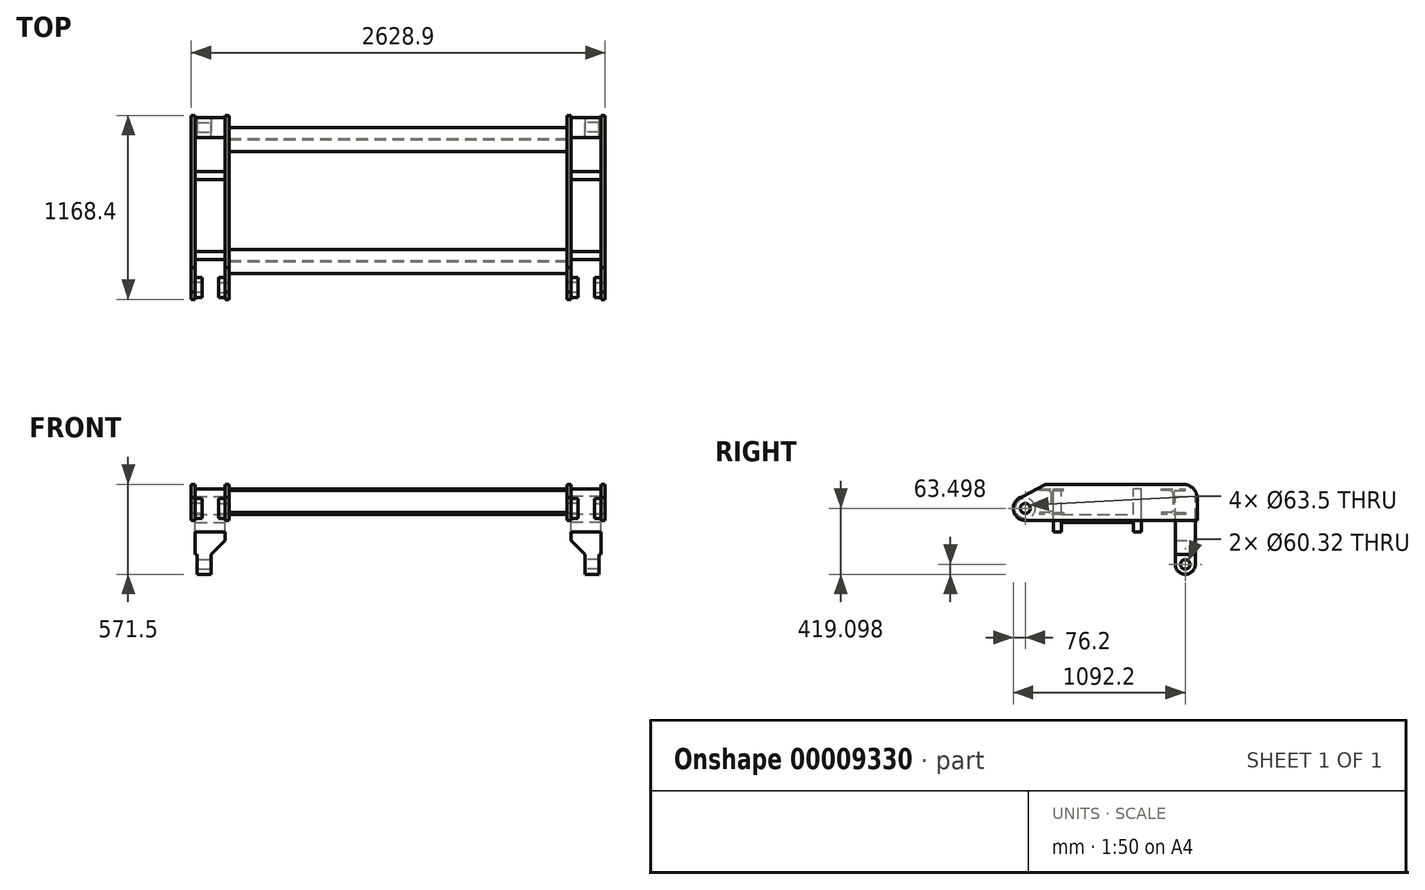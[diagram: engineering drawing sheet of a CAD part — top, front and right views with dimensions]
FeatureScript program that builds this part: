
annotation { "Feature Type Name" : "Feature", "Feature Type Description" : "" }
export const myFeature = defineFeature(function(context is Context, id is Id, definition is map)
    precondition{}
    {
        {
            var Q0;
            Q0=qCreatedBy(makeId("Right.planeOp"),FACE);
            var sketch = newSketch(context, id + "F0", { "sketchPlane" : qUnion([Q0])});
            skLineSegment(sketch, "E0", {"start": v(0, 94.66) * mm, "end": v(0, -108.5) * mm, "construction": true});
            skLineSegment(sketch, "E1.0", {"start": v(387.35, 94.66) * mm, "end": v(387.35, -76.51) * mm, "construction": true});
            skLineSegment(sketch, "E2", {"start": v(387.35, -6.92) * mm, "end": v(515.37, -6.92) * mm, "construction": true});
            skLineSegment(sketch, "E3.0", {"start": v(391.16, 49.98) * mm, "end": v(391.16, -63.81) * mm});
            skLineSegment(sketch, "E4.0", {"start": v(387.35, -87.94) * mm, "end": v(463.55, -87.94) * mm});
            skLineSegment(sketch, "E5.0", {"start": v(403.86, -76.51) * mm, "end": v(463.55, -76.51) * mm});
            skLineSegment(sketch, "E6.trimOffspring", {"start": v(463.55, -76.51) * mm, "end": v(463.55, -87.94) * mm});
            skLineSegment(sketch, "E7.0.MirrorCS", {"start": v(463.55, 62.68) * mm, "end": v(463.55, 74.11) * mm});
            skLineSegment(sketch, "E7.1.MirrorCS", {"start": v(387.35, 74.11) * mm, "end": v(463.55, 74.11) * mm});
            skLineSegment(sketch, "E7.2.MirrorCS", {"start": v(403.86, 62.68) * mm, "end": v(463.55, 62.68) * mm});
            skPoint(sketch, "E8.trimOffspring.end.orphan", {"position": v(387.35, -108.5) * mm});
            skLineSegment(sketch, "E9.0.MirrorCS", {"start": v(311.15, 62.68) * mm, "end": v(311.15, 74.11) * mm});
            skLineSegment(sketch, "E9.1.MirrorCS", {"start": v(311.15, -76.51) * mm, "end": v(311.15, -87.94) * mm});
            skLineSegment(sketch, "E9.2.MirrorCS", {"start": v(387.35, -87.94) * mm, "end": v(311.15, -87.94) * mm});
            skLineSegment(sketch, "E9.3.MirrorCS", {"start": v(383.54, 49.98) * mm, "end": v(383.54, -63.81) * mm});
            skLineSegment(sketch, "E9.4.MirrorCS", {"start": v(387.35, 74.11) * mm, "end": v(311.15, 74.11) * mm});
            skLineSegment(sketch, "E9.5.MirrorCS", {"start": v(370.84, 62.68) * mm, "end": v(311.15, 62.68) * mm});
            skLineSegment(sketch, "E9.6.MirrorCS", {"start": v(370.84, -76.51) * mm, "end": v(311.15, -76.51) * mm});
            skPoint(sketch, "E10.visualSharp", {"position": v(383.54, 62.68) * mm});
            skArc(sketch, "E10.filletArc", {"start": v(383.54, 49.98) * mm, "mid": v(379.82, 58.96) * mm, "end": v(370.84, 62.68) * mm});
            skPoint(sketch, "E11.visualSharp", {"position": v(391.16, 62.68) * mm});
            skArc(sketch, "E11.filletArc", {"start": v(403.86, 62.68) * mm, "mid": v(394.88, 58.96) * mm, "end": v(391.16, 49.98) * mm});
            skPoint(sketch, "E12.visualSharp", {"position": v(383.54, -76.51) * mm});
            skArc(sketch, "E12.filletArc", {"start": v(370.84, -76.51) * mm, "mid": v(379.82, -72.8) * mm, "end": v(383.54, -63.81) * mm});
            skPoint(sketch, "E13.visualSharp", {"position": v(391.16, -76.51) * mm});
            skArc(sketch, "E13.filletArc", {"start": v(391.16, -63.81) * mm, "mid": v(394.88, -72.8) * mm, "end": v(403.86, -76.51) * mm});
            skArc(sketch, "E14.0.MirrorCS", {"start": v(-403.86, 62.68) * mm, "mid": v(-394.88, 58.96) * mm, "end": v(-391.16, 49.98) * mm});
            skArc(sketch, "E14.1.MirrorCS", {"start": v(-391.16, -63.81) * mm, "mid": v(-394.88, -72.8) * mm, "end": v(-403.86, -76.51) * mm});
            skLineSegment(sketch, "E14.2.MirrorCS", {"start": v(-311.15, 62.68) * mm, "end": v(-311.15, 74.11) * mm});
            skArc(sketch, "E14.3.MirrorCS", {"start": v(-383.54, 49.98) * mm, "mid": v(-379.82, 58.96) * mm, "end": v(-370.84, 62.68) * mm});
            skArc(sketch, "E14.4.MirrorCS", {"start": v(-370.84, -76.51) * mm, "mid": v(-379.82, -72.8) * mm, "end": v(-383.54, -63.81) * mm});
            skLineSegment(sketch, "E14.5.MirrorCS", {"start": v(-311.15, -76.51) * mm, "end": v(-311.15, -87.94) * mm});
            skLineSegment(sketch, "E14.6.MirrorCS", {"start": v(-463.55, 62.68) * mm, "end": v(-463.55, 74.11) * mm});
            skLineSegment(sketch, "E14.7.MirrorCS", {"start": v(-463.55, -76.51) * mm, "end": v(-463.55, -87.94) * mm});
            skLineSegment(sketch, "E14.8.MirrorCS", {"start": v(-387.35, 94.66) * mm, "end": v(-387.35, -76.51) * mm, "construction": true});
            skPoint(sketch, "E14.9.MirrorP", {"position": v(-391.16, -76.51) * mm});
            skLineSegment(sketch, "E14.10.MirrorCS", {"start": v(-370.84, -76.51) * mm, "end": v(-311.15, -76.51) * mm});
            skPoint(sketch, "E14.11.MirrorP", {"position": v(-387.35, -108.5) * mm});
            skLineSegment(sketch, "E14.12.MirrorCS", {"start": v(-383.54, 49.98) * mm, "end": v(-383.54, -63.81) * mm});
            skPoint(sketch, "E14.13.MirrorP", {"position": v(-391.16, 62.68) * mm});
            skLineSegment(sketch, "E14.14.MirrorCS", {"start": v(-403.86, 62.68) * mm, "end": v(-463.55, 62.68) * mm});
            skLineSegment(sketch, "E14.15.MirrorCS", {"start": v(-403.86, -76.51) * mm, "end": v(-463.55, -76.51) * mm});
            skLineSegment(sketch, "E14.16.MirrorCS", {"start": v(-370.84, 62.68) * mm, "end": v(-311.15, 62.68) * mm});
            skLineSegment(sketch, "E14.17.MirrorCS", {"start": v(-387.35, 74.11) * mm, "end": v(-463.55, 74.11) * mm});
            skLineSegment(sketch, "E14.18.MirrorCS", {"start": v(-387.35, 74.11) * mm, "end": v(-311.15, 74.11) * mm});
            skPoint(sketch, "E14.19.MirrorP", {"position": v(-383.54, -76.51) * mm});
            skLineSegment(sketch, "E14.20.MirrorCS", {"start": v(-387.35, -87.94) * mm, "end": v(-463.55, -87.94) * mm});
            skPoint(sketch, "E14.21.MirrorP", {"position": v(-383.54, 62.68) * mm});
            skLineSegment(sketch, "E14.22.MirrorCS", {"start": v(-387.35, -87.94) * mm, "end": v(-311.15, -87.94) * mm});
            skLineSegment(sketch, "E14.23.MirrorCS", {"start": v(-391.16, 49.98) * mm, "end": v(-391.16, -63.81) * mm});
            skSolve(sketch);
        }
        {
            var Q0;
            Q0 = qSketchRegion(id + "F0", true);
            extrude(context, id + "F1", {"entities" : qUnion([Q0]), "endBound" : BoundingType.SYMMETRIC, "depth" : 2146.3 * mm});
        }
        {
            var Q0;
            Q0=makeQuery(id+"F1.opExtrude","CAP_FACE",FACE,{"disambiguationData":[OSD([sQuery(id+"F0.wireOp",EDGE,"E14.0.MirrorCS"),sQuery(id+"F0.wireOp",EDGE,"E14.1.MirrorCS"),sQuery(id+"F0.wireOp",EDGE,"E14.2.MirrorCS"),sQuery(id+"F0.wireOp",EDGE,"E14.3.MirrorCS"),sQuery(id+"F0.wireOp",EDGE,"E14.4.MirrorCS"),sQuery(id+"F0.wireOp",EDGE,"E14.5.MirrorCS"),sQuery(id+"F0.wireOp",EDGE,"E14.6.MirrorCS"),sQuery(id+"F0.wireOp",EDGE,"E14.7.MirrorCS"),sQuery(id+"F0.wireOp",EDGE,"E14.10.MirrorCS"),sQuery(id+"F0.wireOp",EDGE,"E14.12.MirrorCS"),sQuery(id+"F0.wireOp",EDGE,"E14.14.MirrorCS"),sQuery(id+"F0.wireOp",EDGE,"E14.15.MirrorCS"),sQuery(id+"F0.wireOp",EDGE,"E14.16.MirrorCS"),sQuery(id+"F0.wireOp",EDGE,"E14.17.MirrorCS"),sQuery(id+"F0.wireOp",EDGE,"E14.18.MirrorCS"),sQuery(id+"F0.wireOp",EDGE,"E14.20.MirrorCS"),sQuery(id+"F0.wireOp",EDGE,"E14.22.MirrorCS"),sQuery(id+"F0.wireOp",EDGE,"E14.23.MirrorCS")])],"isStart":false});
            var sketch = newSketch(context, id + "F2", { "sketchPlane" : qUnion([Q0])});
            skLineSegment(sketch, "E15.0", {"start": v(311.15, 74.11) * mm, "end": v(463.55, 74.11) * mm, "construction": true});
            skLineSegment(sketch, "E16", {"start": v(387.35, 74.11) * mm, "end": v(387.35, -187.68) * mm, "construction": true});
            skLineSegment(sketch, "E17", {"start": v(539.75, 13.66) * mm, "end": v(539.75, -126.04) * mm});
            skLineSegment(sketch, "E18.0", {"start": v(450.85, 102.56) * mm, "end": v(-425.45, 102.56) * mm});
            skPoint(sketch, "E19.visualSharp", {"position": v(539.75, 102.56) * mm});
            skArc(sketch, "E19.filletArc", {"start": v(539.75, 13.66) * mm, "mid": v(513.71, 76.52) * mm, "end": v(450.85, 102.56) * mm});
            skLineSegment(sketch, "E20.0", {"start": v(-628.65, 13.66) * mm, "end": v(-628.65, -213.35) * mm});
            skLineSegment(sketch, "E21.0", {"start": v(-552.45, -49.84) * mm, "end": v(-552.45, -126.04) * mm});
            skLineSegment(sketch, "E22", {"start": v(-424, -87.94) * mm, "end": v(-671.77, -87.94) * mm, "construction": true});
            skLineSegment(sketch, "E23.0", {"start": v(-424, -49.84) * mm, "end": v(-425.45, -49.84) * mm});
            skArc(sketch, "E24", {"start": v(-580.33, 21.07) * mm, "mid": v(-627.32, -64.03) * mm, "end": v(-552.45, -126.04) * mm});
            skLineSegment(sketch, "E25", {"start": v(-425.45, 102.56) * mm, "end": v(-595.1, 13.3) * mm});
            skLineSegment(sketch, "E26", {"start": v(-552.45, -126.04) * mm, "end": v(539.75, -126.04) * mm});
            skLineSegment(sketch, "E27.trimOffspring", {"start": v(-628.65, -49.84) * mm, "end": v(-671.77, -49.84) * mm});
            skCircle(sketch, "E28", {"center": v(-552.45, -49.84) * mm, "radius": 31.75 * mm});
            skSolve(sketch);
        }
        {
            var Q0;
            Q0 = qSketchRegion(id + "F2", true);
            extrude(context, id + "F3", {"entities" : qUnion([Q0]), "depth" : 25.4 * mm});
        }
        {
            var Q0;
            Q0=makeQuery(id+"F3.opExtrude","CAP_FACE",FACE,{"disambiguationData":[OSD([sQuery(id+"F2.wireOp",EDGE,"E17"),sQuery(id+"F2.wireOp",EDGE,"E18.0"),sQuery(id+"F2.wireOp",EDGE,"E19.filletArc"),sQuery(id+"F2.wireOp",EDGE,"E24"),sQuery(id+"F2.wireOp",EDGE,"E25"),sQuery(id+"F2.wireOp",EDGE,"E26"),sQuery(id+"F2.wireOp",EDGE,"E28")])],"isStart":false});
            var sketch = newSketch(context, id + "F4", { "sketchPlane" : qUnion([Q0])});
            skCircle(sketch, "E29", {"center": v(-552.45, -49.84) * mm, "radius": 63.5 * mm});
            skCircle(sketch, "E30.0", {"center": v(-552.45, -49.84) * mm, "radius": 31.75 * mm});
            skSolve(sketch);
        }
        {
            var Q0;
            Q0 = qSketchRegion(id + "F4", true);
            extrude(context, id + "F5", {"entities" : qUnion([Q0]), "operationType" : NewBodyOperationType.ADD, "depth" : 43.69 * mm});
        }
        {
            var Q0;
            Q0=makeQuery(id+"F3.opExtrude","CAP_FACE",FACE,{"disambiguationData":[OSD([sQuery(id+"F2.wireOp",EDGE,"E17"),sQuery(id+"F2.wireOp",EDGE,"E18.0"),sQuery(id+"F2.wireOp",EDGE,"E19.filletArc"),sQuery(id+"F2.wireOp",EDGE,"E24"),sQuery(id+"F2.wireOp",EDGE,"E25"),sQuery(id+"F2.wireOp",EDGE,"E26"),sQuery(id+"F2.wireOp",EDGE,"E28")])],"isStart":false});
            var sketch = newSketch(context, id + "F6", { "sketchPlane" : qUnion([Q0])});
            skLineSegment(sketch, "E31.0", {"start": v(311.15, 74.11) * mm, "end": v(463.55, 74.11) * mm, "construction": true});
            skLineSegment(sketch, "E32", {"start": v(387.35, 74.11) * mm, "end": v(387.35, 301) * mm, "construction": true});
            skLineSegment(sketch, "E33", {"start": v(184.15, 74.11) * mm, "end": v(133.35, 74.11) * mm});
            skLineSegment(sketch, "E34", {"start": v(463.55, 74.11) * mm, "end": v(463.55, 349.58) * mm, "construction": true});
            skLineSegment(sketch, "E35.0", {"start": v(-95.25, 74.11) * mm, "end": v(-95.25, 349.58) * mm, "construction": true});
            skLineSegment(sketch, "E36.0", {"start": v(133.35, -198.94) * mm, "end": v(133.35, -138.74) * mm});
            skLineSegment(sketch, "E37.0", {"start": v(184.15, -198.94) * mm, "end": v(184.15, 74.11) * mm});
            skLineSegment(sketch, "E38.0", {"start": v(184.15, -198.94) * mm, "end": v(133.35, -198.94) * mm});
            skLineSegment(sketch, "E39", {"start": v(-552.45, -49.84) * mm, "end": v(714.62, -49.84) * mm, "construction": true});
            skLineSegment(sketch, "E40.0", {"start": v(-323.85, -138.74) * mm, "end": v(133.35, -138.74) * mm});
            skLineSegment(sketch, "E41.0", {"start": v(-323.85, -87.94) * mm, "end": v(133.35, -87.94) * mm});
            skLineSegment(sketch, "E42.0.MirrorCS", {"start": v(-323.85, -198.94) * mm, "end": v(-323.85, -138.74) * mm});
            skLineSegment(sketch, "E42.1.MirrorCS", {"start": v(-374.65, -198.94) * mm, "end": v(-374.65, 74.11) * mm});
            skLineSegment(sketch, "E42.2.MirrorCS", {"start": v(-374.65, 74.11) * mm, "end": v(-323.85, 74.11) * mm});
            skLineSegment(sketch, "E42.3.MirrorCS", {"start": v(-374.65, -198.94) * mm, "end": v(-323.85, -198.94) * mm});
            skLineSegment(sketch, "E43.trimOffspring", {"start": v(-323.85, -87.94) * mm, "end": v(-323.85, 74.11) * mm});
            skLineSegment(sketch, "E44.trimOffspring", {"start": v(133.35, -87.94) * mm, "end": v(133.35, 74.11) * mm});
            skSolve(sketch);
        }
        {
            var Q0;
            Q0 = qSketchRegion(id + "F6", true);
            extrude(context, id + "F7", {"entities" : qUnion([Q0]), "depth" : 190.5 * mm});
        }
        {
            var Q0;
            Q0=makeQuery(id+"F3.opExtrude","CAP_FACE",FACE,{"disambiguationData":[OSD([sQuery(id+"F2.wireOp",EDGE,"E17"),sQuery(id+"F2.wireOp",EDGE,"E18.0"),sQuery(id+"F2.wireOp",EDGE,"E19.filletArc"),sQuery(id+"F2.wireOp",EDGE,"E24"),sQuery(id+"F2.wireOp",EDGE,"E25"),sQuery(id+"F2.wireOp",EDGE,"E26"),sQuery(id+"F2.wireOp",EDGE,"E28")])],"isStart":false});
            cPlane(context, id + "F8", {"entities" : qUnion([Q0]), "cplaneType" : CPlaneType.OFFSET, "offset" : 95.25 * mm, "width" : 152.4 * mm, "height" : 152.4 * mm});
        }
        {
            var Q0;
            Q0=makeQuery(id+"F3.opExtrude","SWEPT_BODY",BODY,{"disambiguationData":[OSD([sQuery(id+"F2.wireOp",EDGE,"E17"),sQuery(id+"F2.wireOp",EDGE,"E18.0"),sQuery(id+"F2.wireOp",EDGE,"E19.filletArc"),sQuery(id+"F2.wireOp",EDGE,"E24"),sQuery(id+"F2.wireOp",EDGE,"E25"),sQuery(id+"F2.wireOp",EDGE,"E26"),sQuery(id+"F2.wireOp",EDGE,"E28")])]});
            var Q1;
            Q1=qCreatedBy(id+"F8.planeOp",FACE);
            mirror(context, id + "F9", {"entities" : qUnion([Q0]), "mirrorPlane" : qUnion([Q1])});
        }
        {
            var Q0;
            Q0=makeQuery(id+"F3.opExtrude","CAP_FACE",FACE,{"disambiguationData":[OSD([sQuery(id+"F2.wireOp",EDGE,"E17"),sQuery(id+"F2.wireOp",EDGE,"E18.0"),sQuery(id+"F2.wireOp",EDGE,"E19.filletArc"),sQuery(id+"F2.wireOp",EDGE,"E24"),sQuery(id+"F2.wireOp",EDGE,"E25"),sQuery(id+"F2.wireOp",EDGE,"E26"),sQuery(id+"F2.wireOp",EDGE,"E28")])],"isStart":false});
            var sketch = newSketch(context, id + "F10", { "sketchPlane" : qUnion([Q0])});
            skLineSegment(sketch, "E45.0", {"start": v(-323.85, -138.74) * mm, "end": v(133.35, -138.74) * mm, "construction": true});
            skLineSegment(sketch, "E46", {"start": v(-95.25, -138.74) * mm, "end": v(-95.25, -453.43) * mm, "construction": true});
            skLineSegment(sketch, "E47", {"start": v(-552.45, -49.84) * mm, "end": v(812.78, -49.84) * mm, "construction": true});
            skArc(sketch, "E48", {"start": v(400.05, -405.44) * mm, "mid": v(463.55, -468.94) * mm, "end": v(527.05, -405.44) * mm});
            skLineSegment(sketch, "E49.0", {"start": v(400.05, 26.36) * mm, "end": v(527.05, 26.36) * mm});
            skLineSegment(sketch, "E50", {"start": v(527.05, -405.44) * mm, "end": v(527.05, 26.36) * mm});
            skLineSegment(sketch, "E51", {"start": v(400.05, -405.44) * mm, "end": v(400.05, 26.36) * mm});
            skCircle(sketch, "E52", {"center": v(463.55, -405.44) * mm, "radius": 30.16 * mm});
            skSolve(sketch);
        }
        {
            var Q0;
            Q0 = qSketchRegion(id + "F10", true);
            extrude(context, id + "F11", {"entities" : qUnion([Q0]), "operationType" : NewBodyOperationType.ADD, "depth" : 190.5 * mm});
        }
        {
            var Q0;
            Q0=makeQuery(id+"F11.opExtrude","SWEPT_FACE",FACE,{"disambiguationData":[OSD([sQuery(id+"F10.wireOp",EDGE,"E50")])]});
            var sketch = newSketch(context, id + "F12", { "sketchPlane" : qUnion([Q0])});
            skLineSegment(sketch, "E53", {"start": v(0, 0) * mm, "end": v(0, -692.7) * mm, "construction": true});
            skLineSegment(sketch, "E54", {"start": v(-1098.55, -468.94) * mm, "end": v(-1289.05, -468.94) * mm, "construction": true});
            skLineSegment(sketch, "E55.0", {"start": v(-1098.55, -341.94) * mm, "end": v(-1289.05, -341.94) * mm, "construction": true});
            skLineSegment(sketch, "E56.0", {"start": v(1187.45, 0) * mm, "end": v(1187.45, -692.7) * mm, "construction": true});
            skLineSegment(sketch, "E57.0.MirrorCS", {"start": v(-1187.45, 0) * mm, "end": v(-1187.45, -692.7) * mm, "construction": true});
            skLineSegment(sketch, "E58.0", {"start": v(-1276.35, 0) * mm, "end": v(-1276.35, -692.7) * mm, "construction": true});
            skLineSegment(sketch, "E59.bottom", {"start": v(-1289.05, -468.94) * mm, "end": v(-1276.35, -468.94) * mm});
            skLineSegment(sketch, "E59.top", {"start": v(-1289.05, -341.94) * mm, "end": v(-1276.35, -341.94) * mm});
            skLineSegment(sketch, "E59.left", {"start": v(-1289.05, -468.94) * mm, "end": v(-1289.05, -341.94) * mm});
            skLineSegment(sketch, "E59.right", {"start": v(-1276.35, -468.94) * mm, "end": v(-1276.35, -341.94) * mm});
            skLineSegment(sketch, "E60", {"start": v(-1187.45, -468.94) * mm, "end": v(-1187.45, -341.94) * mm});
            skLineSegment(sketch, "E61", {"start": v(-1187.45, -341.94) * mm, "end": v(-1032.6, -187.1) * mm});
            skLineSegment(sketch, "E62", {"start": v(-1032.6, -187.1) * mm, "end": v(-1032.6, -590.93) * mm});
            skLineSegment(sketch, "E63", {"start": v(-1032.6, -590.93) * mm, "end": v(-1187.45, -590.93) * mm});
            skLineSegment(sketch, "E64", {"start": v(-1187.45, -590.93) * mm, "end": v(-1187.45, -468.94) * mm});
            skSolve(sketch);
        }
        {
            var Q0;
            Q0 = qSketchRegion(id + "F12", true);
            extrude(context, id + "F13", {"entities" : qUnion([Q0]), "operationType" : NewBodyOperationType.REMOVE, "endBound" : BoundingType.THROUGH_ALL, "oppositeDirection" : true, "depth" : 25.4 * mm});
        }
        {
            var Q0;
            Q0=makeQuery(id+"F3.opExtrude","SWEPT_BODY",BODY,{"disambiguationData":[OSD([sQuery(id+"F2.wireOp",EDGE,"E17"),sQuery(id+"F2.wireOp",EDGE,"E18.0"),sQuery(id+"F2.wireOp",EDGE,"E19.filletArc"),sQuery(id+"F2.wireOp",EDGE,"E24"),sQuery(id+"F2.wireOp",EDGE,"E25"),sQuery(id+"F2.wireOp",EDGE,"E26"),sQuery(id+"F2.wireOp",EDGE,"E28")])]});
            var Q1;
            Q1=makeQuery(id+"F7.opExtrude","SWEPT_BODY",BODY,{"disambiguationData":[OSD([sQuery(id+"F6.wireOp",EDGE,"E33"),sQuery(id+"F6.wireOp",EDGE,"E36.0"),sQuery(id+"F6.wireOp",EDGE,"E37.0"),sQuery(id+"F6.wireOp",EDGE,"E38.0"),sQuery(id+"F6.wireOp",EDGE,"E40.0"),sQuery(id+"F6.wireOp",EDGE,"E41.0"),sQuery(id+"F6.wireOp",EDGE,"E42.0.MirrorCS"),sQuery(id+"F6.wireOp",EDGE,"E42.1.MirrorCS"),sQuery(id+"F6.wireOp",EDGE,"E42.2.MirrorCS"),sQuery(id+"F6.wireOp",EDGE,"E42.3.MirrorCS"),sQuery(id+"F6.wireOp",EDGE,"E43.trimOffspring"),sQuery(id+"F6.wireOp",EDGE,"E44.trimOffspring")])]});
            var Q2;
            Q2=makeQuery(id+"F9.opPattern","COPY",BODY,{"derivedFrom":makeQuery(id+"F3.opExtrude","SWEPT_BODY",BODY,{"disambiguationData":[OSD([sQuery(id+"F2.wireOp",EDGE,"E17"),sQuery(id+"F2.wireOp",EDGE,"E18.0"),sQuery(id+"F2.wireOp",EDGE,"E19.filletArc"),sQuery(id+"F2.wireOp",EDGE,"E24"),sQuery(id+"F2.wireOp",EDGE,"E25"),sQuery(id+"F2.wireOp",EDGE,"E26"),sQuery(id+"F2.wireOp",EDGE,"E28")])]}),"instanceName":"1"});
            var Q3;
            Q3=qCreatedBy(makeId("Right.planeOp"),FACE);
            mirror(context, id + "F14", {"entities" : qUnion([Q0, Q1, Q2]), "mirrorPlane" : qUnion([Q3])});
        }
    });
